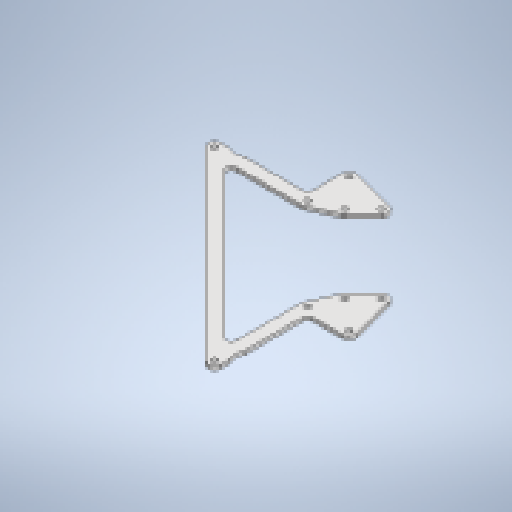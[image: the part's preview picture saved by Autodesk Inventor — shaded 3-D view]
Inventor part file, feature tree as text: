
AUTODESK INVENTOR PART (.ipt)
format: ipt  version: 2025.1 (Build 291241000, 241)  size: 401,408 bytes
history: native  units: mm
features: other x6, extrude x6, sketch x6, reference x4, fillet x3, projected_geometry x2
ambient origin geometry x8: Origin, YZ Plane, XZ Plane, XY Plane, X Axis, Y Axis, Z Axis, Center Point
bodies: Body1 (feature_tree)
feature tree (27):
  other  "ソリッド1"
  extrude  "押し出し1"  Depth=36.0mm
  fillet  "フィレット1"  Radius=2.2mm
  extrude  "押し出し2"  Depth=2.2mm
  other  "作業平面1"
  extrude  "押し出し3"  Depth=5.0mm
  extrude  "押し出し5"  Depth=1.5mm TaperAngle=0.0deg
  fillet  "フィレット2"  Radius=2.0mm
  extrude  "押し出し6"  Depth=16.0mm
  extrude  "押し出し7"  TaperAngle=45.0deg  [1 undecoded]
  fillet  "フィレット3"  Radius=3.0mm
  sketch  "スケッチ1"
  sketch  "スケッチ2"
  projected_geometry  "投影ループ1"
  sketch  "スケッチ3"
  reference  "参照1"
  reference  "参照2"
  projected_geometry  "投影ループ2"
  sketch  "スケッチ4"
  sketch  "スケッチ5"
  reference  "参照3"
  reference  "参照4"
  sketch  "スケッチ6"
  other  "Assembly1"
  other  "senakamata:1"
  other  "KRS2500_scale:1"
  other  "KRS2500_scale:2"
note: 1 required parameter value undecoded (feature->parameter linkage not recoverable at this tier; creation-order binding heuristic only, values carry confidence <= 0.55)
